# Revit family: Table-Casual-Teknion-ATCCD-Circular_Dining-R2015
name_source: partatom
category: Furniture
revit_build: Autodesk Revit Architecture 2015 (Build: 20140323_1530(x64)
units: mm (PartAtom-declared; Revit-internal decimal feet)

## types (2) — shared parameters
Assembly Code = E2020200
Description = Circular Dining Table
Height = 29 "
Manufacturer = Teknion
Manufacturer Fax = 416.661.4586
Part Number = ATCCD
Product Documentation Link = http://www.teknion.com
Product Line = Tables & Collaborative Spaces
Product Page URL = http://www.teknion.com
Series = Tables & Collaborative Spaces
Sustainability Data = http://www.teknion.com
URL = www.teknion.com
Unit Weight URL = http://www.teknion.com
Warranty = http://www.teknion.com

## per-type parameters (varying)
| type | Diameter | Model | Radius |
| 42" Diameter | 42 " | ATCCD42 | 21 " |
| 36" Diameter | 36 " | ATCCD36 | 18 " |

## geometry (parser evidence)
native form markers: Blend x2, Sweep x2
no freeform markers — native parametric forms only
